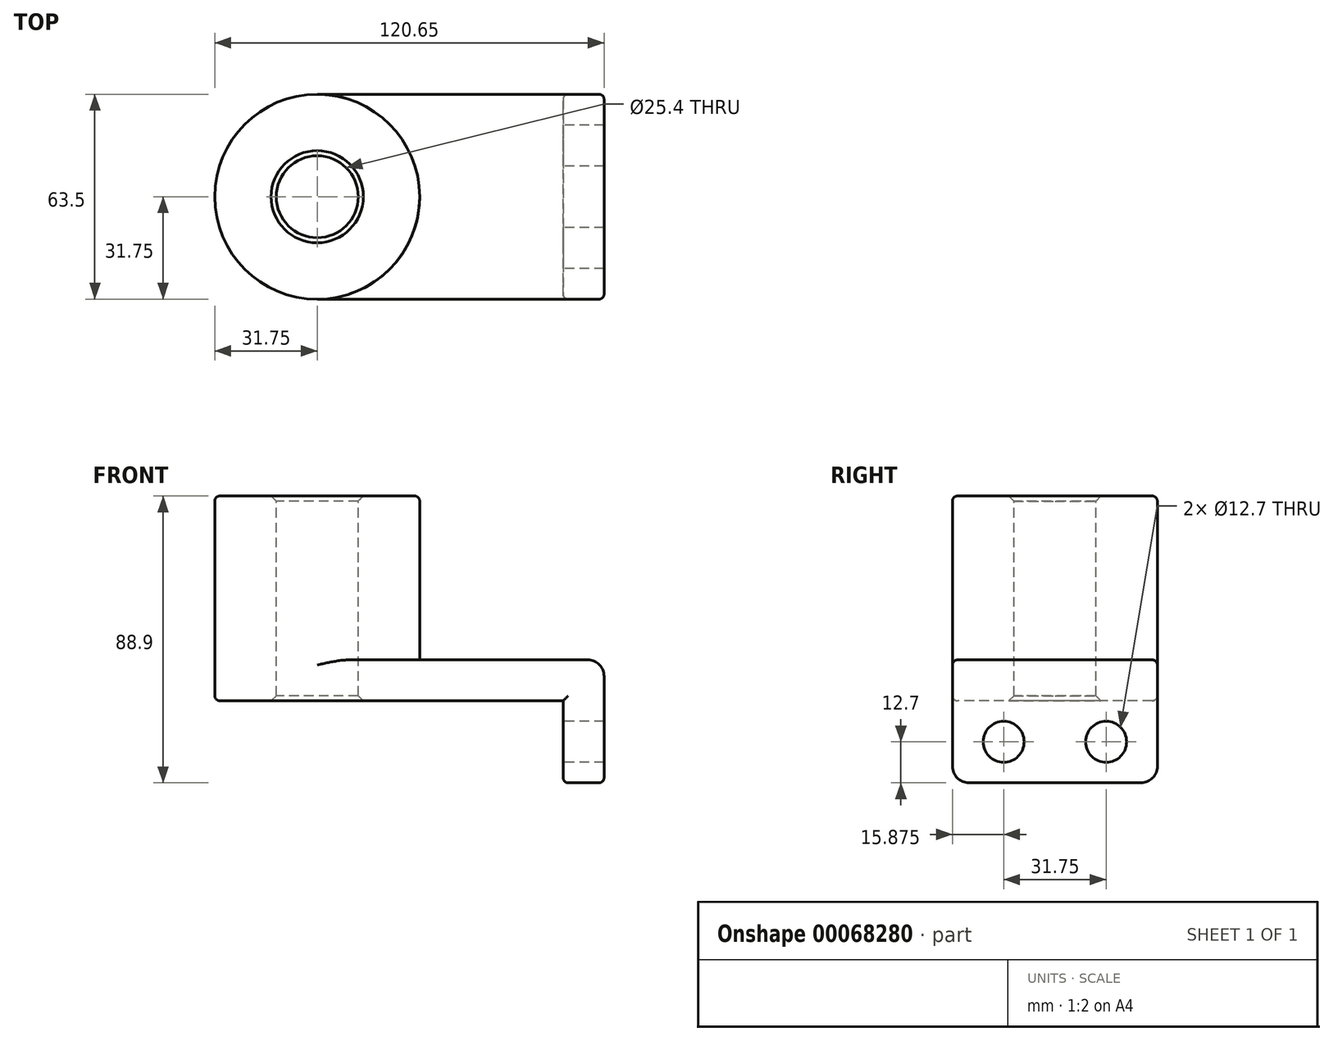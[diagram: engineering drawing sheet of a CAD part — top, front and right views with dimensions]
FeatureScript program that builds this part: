
annotation { "Feature Type Name" : "Feature", "Feature Type Description" : "" }
export const myFeature = defineFeature(function(context is Context, id is Id, definition is map)
    precondition{}
    {
        {
            var Q0;
            Q0=qCreatedBy(makeId("Top.planeOp"),FACE);
            var sketch = newSketch(context, id + "F0", { "sketchPlane" : qUnion([Q0])});
            skLineSegment(sketch, "E0.rect.bottom", {"start": v(38.1, 31.75) * mm, "end": v(-38.1, 31.75) * mm});
            skLineSegment(sketch, "E0.rect.top", {"start": v(38.1, -31.75) * mm, "end": v(-38.1, -31.75) * mm});
            skLineSegment(sketch, "E0.rect.left", {"start": v(38.1, 31.75) * mm, "end": v(38.1, -31.75) * mm});
            skLineSegment(sketch, "E0.rect.right", {"start": v(-38.1, 31.75) * mm, "end": v(-38.1, -31.75) * mm});
            skPoint(sketch, "E0.rect.middle", {"position": v(0, 0) * mm});
            skCircle(sketch, "E1", {"center": v(-38.1, 0) * mm, "radius": 31.75 * mm});
            skCircle(sketch, "E2", {"center": v(-38.1, 0) * mm, "radius": 12.7 * mm});
            skSolve(sketch);
        }
        {
            var Q0;
            {var subQ1=sQuery(id+"F0.wireOp",EDGE,"E0.rect.right");var subQ3=sQuery(id+"F0.wireOp",EDGE,"E2");var subQ4=makeQuery(id+"F0.imprint","INTERSECT",VERTEX,{"disambiguationData":[OD(0.0)],"derivedFrom":[subQ1,subQ3]});Q0=makeQuery(id+"F0.imprint","IMPRINT",FACE,{"disambiguationData":[TD([[makeQuery(id+"F0.imprint","IMPRINT",EDGE,{"disambiguationData":[TD([[subQ4,-1.0]])],"derivedFrom":subQ3}),-1.0]])]});}
            var Q1;
            {var subQ0=sQuery(id+"F0.wireOp",EDGE,"E0.rect.bottom");Q1=makeQuery(id+"F0.imprint","IMPRINT",FACE,{"disambiguationData":[TD([[makeQuery(id+"F0.imprint","IMPRINT",EDGE,{"derivedFrom":subQ0}),1.0]])]});}
            var Q2;
            {var subQ1=sQuery(id+"F0.wireOp",EDGE,"E0.rect.right");var subQ3=sQuery(id+"F0.wireOp",EDGE,"E2");var subQ4=makeQuery(id+"F0.imprint","INTERSECT",VERTEX,{"disambiguationData":[OD(0.0)],"derivedFrom":[subQ1,subQ3]});Q2=makeQuery(id+"F0.imprint","IMPRINT",FACE,{"disambiguationData":[TD([[makeQuery(id+"F0.imprint","IMPRINT",EDGE,{"disambiguationData":[TD([[subQ4,1.0]])],"derivedFrom":subQ3}),-1.0]])]});}
            extrude(context, id + "F1", {"entities" : qUnion([Q0, Q1, Q2]), "oppositeDirection" : true, "depth" : 12.7 * mm});
        }
        {
            var Q0;
            {var subQ1=sQuery(id+"F0.wireOp",EDGE,"E0.rect.right");var subQ3=sQuery(id+"F0.wireOp",EDGE,"E2");var subQ4=makeQuery(id+"F0.imprint","INTERSECT",VERTEX,{"disambiguationData":[OD(0.0)],"derivedFrom":[subQ1,subQ3]});Q0=makeQuery(id+"F0.imprint","IMPRINT",FACE,{"disambiguationData":[TD([[makeQuery(id+"F0.imprint","IMPRINT",EDGE,{"disambiguationData":[TD([[subQ4,1.0]])],"derivedFrom":subQ3}),-1.0]])]});}
            var Q1;
            {var subQ1=sQuery(id+"F0.wireOp",EDGE,"E0.rect.right");var subQ3=sQuery(id+"F0.wireOp",EDGE,"E2");var subQ4=makeQuery(id+"F0.imprint","INTERSECT",VERTEX,{"disambiguationData":[OD(0.0)],"derivedFrom":[subQ1,subQ3]});Q1=makeQuery(id+"F0.imprint","IMPRINT",FACE,{"disambiguationData":[TD([[makeQuery(id+"F0.imprint","IMPRINT",EDGE,{"disambiguationData":[TD([[subQ4,-1.0]])],"derivedFrom":subQ3}),-1.0]])]});}
            extrude(context, id + "F2", {"entities" : qUnion([Q0, Q1]), "operationType" : NewBodyOperationType.ADD, "depth" : 50.8 * mm});
        }
        {
            var Q0;
            Q0=makeQuery(id+"F1.opExtrude","SWEPT_FACE",FACE,{"disambiguationData":[OSD([sQuery(id+"F0.wireOp",EDGE,"E0.rect.left")])]});
            var sketch = newSketch(context, id + "F3", { "sketchPlane" : qUnion([Q0])});
            skLineSegment(sketch, "E3.bottom", {"start": v(-31.75, 0) * mm, "end": v(31.75, 0) * mm});
            skLineSegment(sketch, "E3.top", {"start": v(-31.75, -38.1) * mm, "end": v(31.75, -38.1) * mm});
            skLineSegment(sketch, "E3.left", {"start": v(-31.75, 0) * mm, "end": v(-31.75, -38.1) * mm});
            skLineSegment(sketch, "E3.right", {"start": v(31.75, 0) * mm, "end": v(31.75, -38.1) * mm});
            skLineSegment(sketch, "E4", {"start": v(0, -12.7) * mm, "end": v(0, -38.1) * mm, "construction": true});
            skCircle(sketch, "E5", {"center": v(-15.87, -25.4) * mm, "radius": 6.35 * mm});
            skCircle(sketch, "E6.MirrorC", {"center": v(15.87, -25.4) * mm, "radius": 6.35 * mm});
            skSolve(sketch);
        }
        {
            var Q0;
            {var subQ2=sQuery(id+"F3.wireOp",EDGE,"E3.top");Q0=makeQuery(id+"F3.imprint","IMPRINT",FACE,{"disambiguationData":[TD([[makeQuery(id+"F3.imprint","IMPRINT",EDGE,{"derivedFrom":subQ2}),1.0]])]});}
            var Q1;
            {var subQ0=sQuery(id+"F3.wireOp",EDGE,"E3.bottom");Q1=makeQuery(id+"F3.imprint","IMPRINT",FACE,{"disambiguationData":[TD([[makeQuery(id+"F3.imprint","IMPRINT",EDGE,{"derivedFrom":subQ0}),1.0]])]});}
            extrude(context, id + "F4", {"entities" : qUnion([Q0, Q1]), "operationType" : NewBodyOperationType.ADD, "depth" : 12.7 * mm});
        }
        {
            var Q0;
            Q0=makeQuery(id+"F2.opExtrude","CAP_EDGE",EDGE,{"disambiguationData":[OSD([sQuery(id+"F0.wireOp",EDGE,"E1")])],"isStart":true});
            var Q1;
            Q1=makeQuery(id+"F4.opExtrude","CAP_EDGE",EDGE,{"disambiguationData":[OSD([sQuery(id+"F3.wireOp",EDGE,"E3.bottom")])],"isStart":false});
            var Q2;
            Q2=makeQuery(id+"F4.opExtrude","SWEPT_EDGE",EDGE,{"disambiguationData":[OSD([sQuery(id+"F3.wireOp",EDGE,"E3.top"),sQuery(id+"F3.wireOp",EDGE,"E3.left")])]});
            var Q3;
            Q3=makeQuery(id+"F4.opExtrude","SWEPT_EDGE",EDGE,{"disambiguationData":[OSD([sQuery(id+"F3.wireOp",EDGE,"E3.top"),sQuery(id+"F3.wireOp",EDGE,"E3.right")])]});
            fillet(context, id + "F5", {"entities" : qUnion([Q0, Q1, Q2, Q3]), "radius" : 5.08 * mm, "tangentPropagation" : true, "allowEdgeOverflow" : false});
        }
        {
            var Q0;
            {var subQ0=sQuery(id+"F0.wireOp",EDGE,"E2");Q0=makeQuery(id+"F2.boolean.opBoolean","MERGE",FACE,{"derivedFrom":[makeQuery(id+"F1.opExtrude","SWEPT_FACE",FACE,{"disambiguationData":[OSD([subQ0])]}),makeQuery(id+"F2.opExtrude","SWEPT_FACE",FACE,{"disambiguationData":[OSD([subQ0])]})]});}
            chamfer(context, id + "F6", {"entities" : qUnion([Q0]), "width" : 1.59 * mm, "tangentPropagation" : true});
        }
        {
            var Q0;
            Q0=makeQuery(id+"F4.boolean.opBoolean","MERGE",EDGE,{"derivedFrom":[makeQuery(id+"F1.opExtrude","CAP_EDGE",EDGE,{"disambiguationData":[OSD([sQuery(id+"F0.wireOp",EDGE,"E0.rect.bottom")])],"isStart":true}),makeQuery(id+"F4.opExtrude","SWEPT_EDGE",EDGE,{"disambiguationData":[OSD([sQuery(id+"F3.wireOp",EDGE,"E3.bottom"),sQuery(id+"F3.wireOp",EDGE,"E3.right")])]})]});
            var Q1;
            Q1=makeQuery(id+"F1.opExtrude","CAP_EDGE",EDGE,{"disambiguationData":[OSD([sQuery(id+"F0.wireOp",EDGE,"E0.rect.bottom")])],"isStart":false});
            var Q2;
            Q2=makeQuery(id+"F4.opExtrude","CAP_EDGE",EDGE,{"disambiguationData":[OSD([sQuery(id+"F3.wireOp",EDGE,"E3.right")])],"isStart":true});
            var Q3;
            Q3=makeQuery(id+"F2.opExtrude","CAP_EDGE",EDGE,{"disambiguationData":[OSD([sQuery(id+"F0.wireOp",EDGE,"E1")])],"isStart":false});
            fillet(context, id + "F7", {"entities" : qUnion([Q0, Q1, Q2, Q3]), "radius" : 1.59 * mm, "tangentPropagation" : true, "allowEdgeOverflow" : false});
        }
    });
